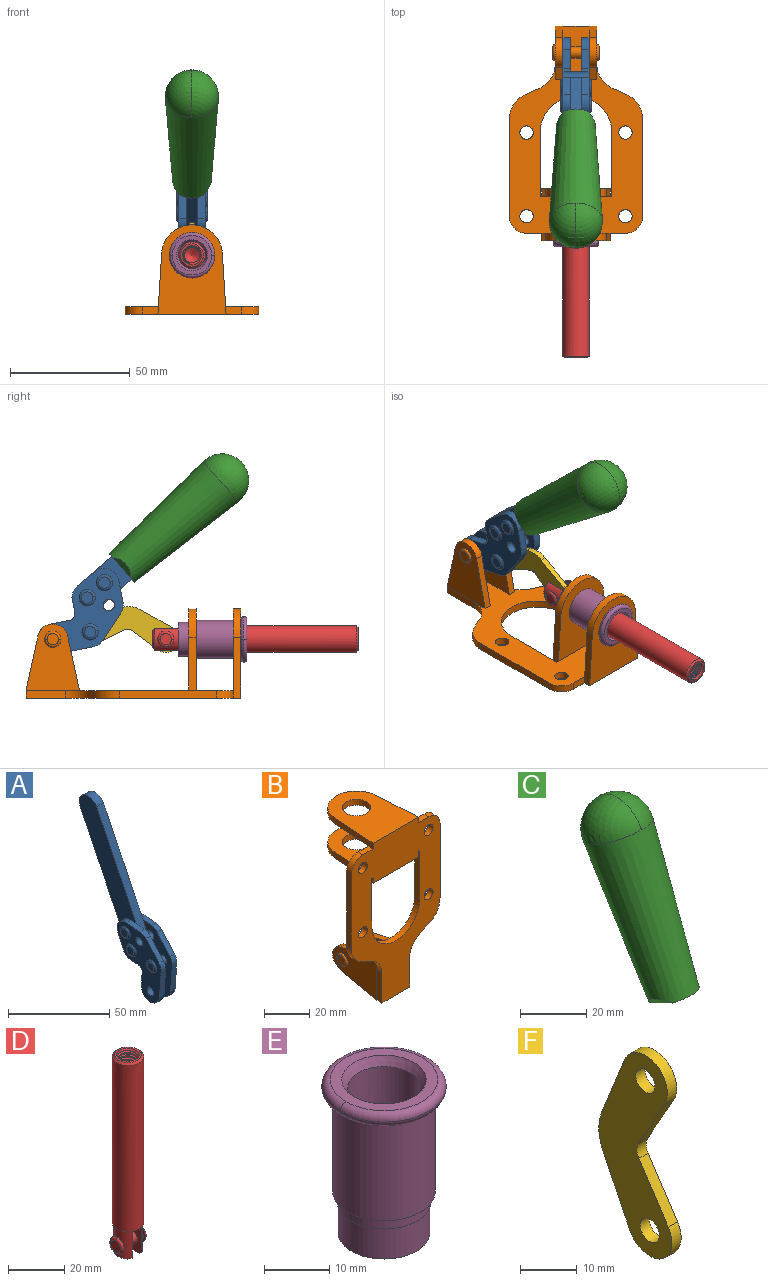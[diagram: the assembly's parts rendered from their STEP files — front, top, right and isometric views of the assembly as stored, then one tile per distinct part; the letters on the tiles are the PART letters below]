
ASSEMBLY  parts=6 mates=6
PART A: 59 faces, bbox 12.9x60.2x99.6 mm
  f0: torus R=2.39mm, axis (-1,0,0), area 14.9mm2, adj f20,f43,f51
  f1: torus R=2.39mm, axis (-1,0,0), area 14.9mm2, adj f19,f42,f51
  f2: torus R=2.39mm, axis (-1,0,0), area 14.9mm2, adj f18,f35,f51
  f3: torus R=2.39mm, axis (-1,0,0), area 14.9mm2, adj f14,f17,f23
  f4: torus R=2.39mm, axis (-1,0,0), area 14.9mm2, adj f13,f16,f23
  f5: torus R=2.39mm, axis (-1,0,0), area 14.9mm2, adj f12,f15,f23
  f6: cylinder r=2.39mm len=4.78mm, axis (1,0,0), area 46.5mm2, adj f48,f50,f51
  f7: cylinder r=2.39mm len=4.78mm, axis (1,0,0), area 46.5mm2, adj f50,f51
  f8: cylinder r=6.35mm len=12.68mm, axis (1,0,0), area 61.8mm2, adj f38,f39,f50,f51
  f9: cylinder r=2.39mm len=4.78mm, axis (-1,0,0), area 70.5mm2, adj f46,f50
  f10: cylinder r=2.39mm len=4.78mm, axis (-1,0,0), area 46.5mm2, adj f23,f45,f46
  f11: cylinder r=2.39mm len=4.78mm, axis (-1,0,0), area 46.5mm2, adj f23,f46
  f12: plane 4.78x4.78mm, normal (1,0,0), area 17.9mm2, adj f5,f15
  f13: plane 4.78x4.78mm, normal (1,0,0), area 17.9mm2, adj f4,f16
  f14: plane 4.78x4.78mm, normal (1,0,0), area 17.9mm2, adj f3,f17
  f15: torus R=2.39mm, axis (-1,0,0), area 14.9mm2, adj f5,f12,f23
  f16: torus R=2.39mm, axis (-1,0,0), area 14.9mm2, adj f4,f13,f23
  f17: torus R=2.39mm, axis (-1,0,0), area 14.9mm2, adj f3,f14,f23
  f18: plane 4.78x4.78mm, normal (-1,0,0), area 17.9mm2, adj f2,f35
  f19: plane 4.78x4.78mm, normal (-1,0,0), area 17.9mm2, adj f1,f42
  f20: plane 4.78x4.78mm, normal (-1,0,0), area 17.9mm2, adj f0,f43
  f21: plane 2.26x0.2mm, normal (1,0,0), area 0.2mm2, adj f31,f44
  f22: plane 2.26x0.2mm, normal (-1,0,0), area 0.2mm2, adj f41,f44
  f23: plane 39.37x30.77mm, normal (1,0,0), area 565.5mm2, adj f3,f4,f5,f10,f11,f15,f16,f17
  f24: cylinder r=6.1mm len=4.15mm, axis (-1,0,0), area 14.7mm2, adj f23,f25,f32,f46
  f25: plane 10.25x9.01mm, normal (0,-0.75,0.66), area 42.3mm2, adj f23,f24,f26,f46
  f26: cylinder r=6.35mm len=4.64mm, axis (-1,0,0), area 15.6mm2, adj f23,f25,f27,f46
  f27: plane 15.84x3.1mm, normal (0,-1,-0.07), area 49.2mm2, adj f23,f26,f28,f46
  f28: cylinder r=6.35mm len=12.68mm, axis (-1,0,0), area 61.8mm2, adj f23,f27,f29,f46
  f29: plane 8.11x3.1mm, normal (0,1,0.07), area 25.2mm2, adj f23,f28,f30,f46
  f30: cylinder r=3.05mm len=3.25mm, axis (-1,0,0), area 14.8mm2, adj f23,f29,f31,f46
  f31: plane 5.99x3.1mm, normal (0,0.07,-1), area 18.6mm2, adj f21,f23,f30,f44,f46
  f32: plane 9.5x3.1mm, normal (0,-0.07,1), area 29.5mm2, adj f23,f24,f33,f46,f47
  f33: cylinder r=6.1mm len=8.63mm, axis (-1,0,0), area 39.1mm2, adj f23,f32,f34,f47
  f34: plane 8.65x3.96mm, normal (0,0.91,-0.42), area 29.5mm2, adj f23,f33,f44,f47
  f35: torus R=2.39mm, axis (-1,0,0), area 14.9mm2, adj f2,f18,f51
  f36: plane 10.25x9.01mm, normal (0,-0.75,0.66), area 42.3mm2, adj f37,f49,f50,f51
  f37: cylinder r=6.35mm len=4.64mm, axis (1,0,0), area 15.6mm2, adj f36,f38,f50,f51
  f38: plane 15.84x3.1mm, normal (0,-1,-0.07), area 49.2mm2, adj f8,f37,f50,f51
  f39: plane 8.11x3.1mm, normal (0,1,0.07), area 25.2mm2, adj f8,f40,f50,f51
  f40: cylinder r=3.05mm len=3.25mm, axis (1,0,0), area 14.8mm2, adj f39,f41,f50,f51
  f41: plane 5.99x3.1mm, normal (0,0.07,-1), area 18.6mm2, adj f22,f40,f44,f50,f51
  f42: torus R=2.39mm, axis (-1,0,0), area 14.9mm2, adj f1,f19,f51
  f43: torus R=2.39mm, axis (-1,0,0), area 14.9mm2, adj f0,f20,f51
  f44: cylinder r=6.35mm len=12.12mm, axis (-1,0,0), area 128.9mm2, adj f21,f22,f23,f31,f34,f41,f46,f47
  f45: plane 2.65x1.35mm, normal (1,0,0), area 1mm2, adj f10,f55
  f46: plane 39.08x20.42mm, normal (-1,0,0), area 412.5mm2, adj f9,f10,f11,f24,f25,f26,f27,f28
  f47: plane 77.62x39.82mm, normal (1,0,0), area 850mm2, adj f32,f33,f34,f44,f53,f54,f55
  f48: plane 2.65x1.35mm, normal (-1,0,0), area 1mm2, adj f6,f55
  f49: cylinder r=6.1mm len=4.15mm, axis (1,0,0), area 14.7mm2, adj f36,f50,f51,f56
  f50: plane 39.08x20.42mm, normal (1,0,0), area 412.5mm2, adj f6,f7,f8,f9,f36,f37,f38,f39
  f51: plane 39.37x30.77mm, normal (-1,0,0), area 565.5mm2, adj f0,f1,f2,f6,f7,f8,f35,f36
  f52: plane 8.65x3.96mm, normal (0,0.91,-0.42), area 29.5mm2, adj f44,f51,f57,f58
  f53: plane 68.49x33.4mm, normal (0,0.9,-0.44), area 358.1mm2, adj f44,f47,f54,f58
  f54: cylinder r=6.35mm len=12.06mm, axis (1,0,0), area 93.7mm2, adj f47,f53,f55,f58
  f55: plane 68.49x33.4mm, normal (0,-0.9,0.44), area 358.1mm2, adj f44,f45,f46,f47,f48,f50,f54,f58
  f56: plane 9.5x3.1mm, normal (0,-0.07,1), area 29.5mm2, adj f49,f50,f51,f57,f58
  f57: cylinder r=6.1mm len=8.63mm, axis (1,0,0), area 39.1mm2, adj f51,f52,f56,f58
  f58: plane 77.62x39.82mm, normal (-1,0,0), area 850mm2, adj f44,f52,f53,f54,f55,f56,f57
PART B: 55 faces, bbox 55.7x37.4x89.8 mm
  f0: torus R=2.41mm, axis (-1,0,0), area 15mm2, adj f11,f15,f25
  f1: torus R=2.41mm, axis (-1,0,0), area 15mm2, adj f10,f12,f22
  f2: cylinder r=2.78mm len=5.56mm, axis (0,-1,0), area 54.2mm2, adj f30,f54
  f3: cylinder r=14.99mm len=29.97mm, axis (0,-1,0), area 145.9mm2, adj f30,f49,f53,f54
  f4: cylinder r=2.78mm len=5.56mm, axis (0,-1,0), area 54.2mm2, adj f30,f54
  f5: cylinder r=2.78mm len=5.56mm, axis (0,-1,0), area 54.2mm2, adj f30,f54
  f6: cylinder r=2.78mm len=5.56mm, axis (0,-1,0), area 54.2mm2, adj f30,f54
  f7: cylinder r=6.35mm len=12.7mm, axis (0,0,1), area 123.6mm2, adj f27,f51
  f8: cylinder r=6.35mm len=12.7mm, axis (0,0,-1), area 124.7mm2, adj f21,f35
  f9: cylinder r=2.41mm len=11.18mm, axis (-1,0,0), area 169.4mm2, adj f16,f19
  f10: plane 4.83x4.83mm, normal (1,0,0), area 18.3mm2, adj f1,f12
  f11: plane 4.83x4.83mm, normal (-1,0,0), area 18.3mm2, adj f0,f15
  f12: torus R=2.41mm, axis (-1,0,0), area 15mm2, adj f1,f10,f22
  f13: cylinder r=6.35mm len=12.41mm, axis (1,0,0), area 53.4mm2, adj f18,f19,f22,f23
  f14: cylinder r=6.35mm len=12.41mm, axis (-1,0,0), area 53.4mm2, adj f16,f17,f24,f25
  f15: torus R=2.41mm, axis (-1,0,0), area 15mm2, adj f0,f11,f25
  f16: plane 27.86x22.35mm, normal (1,0,0), area 425.4mm2, adj f9,f14,f17,f24,f30
  f17: plane 22.86x4.97mm, normal (0,0.21,0.98), area 72.5mm2, adj f14,f16,f25,f30
  f18: plane 22.86x4.97mm, normal (0,0.21,0.98), area 72.5mm2, adj f13,f19,f22,f30
  f19: plane 27.86x22.35mm, normal (-1,0,0), area 425.4mm2, adj f9,f13,f18,f23,f30
  f20: cylinder r=12.7mm len=25.35mm, axis (0,0,-1), area 119.8mm2, adj f21,f34,f35,f36
  f21: plane 34.21x28.07mm, normal (0,0,-1), area 702.4mm2, adj f8,f20,f30,f34,f36
  f22: plane 27.96x22.45mm, normal (1,0,0), area 407.2mm2, adj f1,f12,f13,f18,f23,f30,f42,f43
  f23: plane 22.86x4.97mm, normal (0,0.21,-0.98), area 72.5mm2, adj f13,f19,f22,f44
  f24: plane 22.86x4.97mm, normal (0,0.21,-0.98), area 72.5mm2, adj f14,f16,f25,f44
  f25: plane 27.86x22.35mm, normal (-1,0,0), area 407.1mm2, adj f0,f14,f15,f17,f24,f30,f45,f46
  f26: plane 3.1x0.95mm, normal (0,0,-1), area 2.7mm2, adj f30,f49,f50,f54
  f27: plane 34.21x28.07mm, normal (0,0,1), area 702.4mm2, adj f7,f28,f30,f50,f52
  f28: cylinder r=12.7mm len=25.35mm, axis (0,0,1), area 118.8mm2, adj f27,f50,f51,f52
  f29: plane 3.1x0.95mm, normal (0,0,-1), area 2.7mm2, adj f30,f52,f53,f54
  f30: plane 86.54x55.63mm, normal (0,1,0), area 2362.9mm2, adj f2,f3,f4,f5,f6,f16,f17,f18
  f31: plane 40.56x3.1mm, normal (-1,0,0), area 125.7mm2, adj f30,f32,f48,f54
  f32: cylinder r=7.11mm len=7.11mm, axis (0,-1,0), area 34.6mm2, adj f30,f31,f33,f54
  f33: plane 6.67x3.1mm, normal (0,0,1), area 20.4mm2, adj f30,f32,f34,f54
  f34: plane 25.39x3.13mm, normal (-1,0.06,0), area 79.5mm2, adj f20,f21,f33,f35,f54
  f35: plane 37.31x28.45mm, normal (0,0,1), area 789.9mm2, adj f8,f20,f34,f36,f54
  f36: plane 25.39x3.13mm, normal (1,0.06,0), area 79.5mm2, adj f20,f21,f35,f37,f54
  f37: plane 6.67x3.1mm, normal (0,0,1), area 20.4mm2, adj f30,f36,f38,f54
  f38: cylinder r=7.11mm len=7.11mm, axis (0,-1,0), area 34.6mm2, adj f30,f37,f39,f54
  f39: plane 40.56x3.1mm, normal (1,0,0), area 125.7mm2, adj f30,f38,f40,f54
  f40: cylinder r=11.18mm len=10.16mm, axis (0,-1,0), area 39.5mm2, adj f30,f39,f41,f54
  f41: plane 6.09x3.1mm, normal (0.42,0,-0.91), area 20.8mm2, adj f30,f40,f42,f54
  f42: cylinder r=11.18mm len=9.41mm, axis (0,-1,0), area 37.2mm2, adj f22,f30,f41,f43,f54
  f43: plane 16.5x3.1mm, normal (1,0,0), area 51.1mm2, adj f22,f42,f44,f54
  f44: plane 17.37x3.1mm, normal (0,0,-1), area 53.8mm2, adj f23,f24,f30,f43,f45,f54
  f45: plane 16.5x3.1mm, normal (-1,0,0), area 51.1mm2, adj f25,f44,f46,f54
  f46: cylinder r=11.18mm len=9.41mm, axis (0,-1,0), area 37.2mm2, adj f25,f30,f45,f47,f54
  f47: plane 6.09x3.1mm, normal (-0.42,0,-0.91), area 20.8mm2, adj f30,f46,f48,f54
  f48: cylinder r=11.18mm len=10.16mm, axis (0,-1,0), area 39.5mm2, adj f30,f31,f47,f54
  f49: plane 26.54x3.1mm, normal (-1,0,0), area 82.3mm2, adj f3,f26,f30,f54
  f50: plane 25.39x3.1mm, normal (1,0.06,0), area 78.8mm2, adj f26,f27,f28,f51,f54
  f51: plane 37.31x28.45mm, normal (0,0,-1), area 789.9mm2, adj f7,f28,f50,f52,f54
  f52: plane 25.39x3.1mm, normal (-1,0.06,0), area 78.8mm2, adj f27,f28,f29,f51,f54
  f53: plane 26.54x3.1mm, normal (1,0,0), area 82.3mm2, adj f3,f29,f30,f54
  f54: plane 89.66x55.63mm, normal (0,-1,0), area 2678.5mm2, adj f2,f3,f4,f5,f6,f26,f29,f31
PART C: 11 faces, bbox 22.3x42.6x64.5 mm
  f0: sphere r=11.13mm, area 411.4mm2, adj f1,f8
  f1: cone r=11.11mm half-angle=3.3deg, axis (0,0.44,0.9), area 3251.8mm2, adj f0,f7,f8,f9,f10
  f2: cylinder r=6.16mm len=11.7mm, axis (1,0,0), area 89.5mm2, adj f3,f4,f5,f6
  f3: plane 60.23x36.75mm, normal (-1,0,0), area 763.6mm2, adj f2,f4,f6,f10
  f4: plane 51.37x25.05mm, normal (0,0.9,-0.44), area 264.2mm2, adj f2,f3,f5,f10
  f5: plane 60.23x36.75mm, normal (1,0,0), area 763.6mm2, adj f2,f4,f6,f10
  f6: plane 51.37x25.05mm, normal (0,-0.9,0.44), area 264.2mm2, adj f2,f3,f5,f10
  f7: plane 9.95x5.95mm, normal (0.71,-0.31,-0.64), area 25.8mm2, adj f1,f10
  f8: sphere r=11.13mm, area 411.4mm2, adj f0,f1
  f9: plane 9.95x5.95mm, normal (-0.71,-0.31,-0.64), area 25.8mm2, adj f1,f10
  f10: plane 14.27x11.38mm, normal (0,-0.44,-0.9), area 106.7mm2, adj f1,f3,f4,f5,f6,f7,f9
PART D: 48 faces, bbox 12.6x11.1x86.1 mm
  f0: torus R=2.41mm, axis (-1,0,0), area 15mm2, adj f30,f32,f34
  f1: torus R=2.41mm, axis (-1,0,0), area 15mm2, adj f29,f31,f33
  f2: cylinder r=5.54mm len=72.39mm, axis (0,0,1), area 2518.5mm2, adj f3,f4,f42,f43
  f3: cone r=5.54mm half-angle=45deg, axis (0,0,1), area 7.6mm2, adj f2,f5,f41
  f4: cone r=5.54mm half-angle=45deg, axis (0,0,-1), area 34.9mm2, adj f2,f39
  f5: cylinder r=5.08mm len=11.48mm, axis (0,0,1), area 108.3mm2, adj f3,f7,f8,f41
  f6: cylinder r=2.41mm len=4.83mm, axis (-1,0,0), area 71.2mm2, adj f40,f41
  f7: cylinder r=2.41mm len=4.83mm, axis (-1,0,0), area 7.6mm2, adj f5,f34
  f8: cone r=5.08mm half-angle=45deg, axis (0,0,1), area 10.6mm2, adj f5,f37,f41
  f9: cone r=3.98mm half-angle=45deg, axis (0,0,1), area 17.6mm2, adj f27,f39,f45,f46,f47
  f10: cylinder r=2.41mm len=4.83mm, axis (-1,0,0), area 7.6mm2, adj f33,f38
  f11: cylinder r=3.2mm len=6.4mm, axis (0,0,1), area 78.4mm2, adj f12,f28,f44,f45,f47
  f12: cylinder r=3.2mm len=6.4mm, axis (0,0,1), area 10.5mm2, adj f11,f13,f45,f47
  f13: cylinder r=3.2mm len=6.4mm, axis (0,0,1), area 10.5mm2, adj f12,f14,f45,f47
  f14: cylinder r=3.2mm len=6.4mm, axis (0,0,1), area 10.5mm2, adj f13,f15,f45,f47
  f15: cylinder r=3.2mm len=6.4mm, axis (0,0,1), area 10.5mm2, adj f14,f16,f45,f47
  f16: cylinder r=3.2mm len=6.4mm, axis (0,0,1), area 10.5mm2, adj f15,f17,f45,f47
  f17: cylinder r=3.2mm len=6.4mm, axis (0,0,1), area 10.5mm2, adj f16,f18,f45,f47
  f18: cylinder r=3.2mm len=6.4mm, axis (0,0,1), area 10.5mm2, adj f17,f19,f45,f47
  f19: cylinder r=3.2mm len=6.4mm, axis (0,0,1), area 10.5mm2, adj f18,f20,f45,f47
  f20: cylinder r=3.2mm len=6.4mm, axis (0,0,1), area 10.5mm2, adj f19,f21,f45,f47
  f21: cylinder r=3.2mm len=6.4mm, axis (0,0,1), area 10.5mm2, adj f20,f22,f45,f47
  f22: cylinder r=3.2mm len=6.4mm, axis (0,0,1), area 10.5mm2, adj f21,f23,f45,f47
  f23: cylinder r=3.2mm len=6.4mm, axis (0,0,1), area 10.5mm2, adj f22,f24,f45,f47
  f24: cylinder r=3.2mm len=6.4mm, axis (0,0,1), area 10.5mm2, adj f23,f25,f45,f47
  f25: cylinder r=3.2mm len=6.4mm, axis (0,0,1), area 10.5mm2, adj f24,f26,f45,f47
  f26: cylinder r=3.2mm len=6.4mm, axis (0,0,1), area 10.5mm2, adj f25,f27,f45,f47
  f27: cylinder r=3.2mm len=6.4mm, axis (0,0,1), area 7.4mm2, adj f9,f26,f45,f47
  f28: cone r=3.2mm half-angle=60deg, axis (0,0,1), area 37.2mm2, adj f11
  f29: plane 4.83x4.83mm, normal (-1,0,0), area 18.3mm2, adj f1,f31
  f30: plane 4.83x4.83mm, normal (1,0,0), area 18.3mm2, adj f0,f32
  f31: torus R=2.41mm, axis (-1,0,0), area 15mm2, adj f1,f29,f33
  f32: torus R=2.41mm, axis (-1,0,0), area 15mm2, adj f0,f30,f34
  f33: plane 6.83x6.83mm, normal (1,0,0), area 18.3mm2, adj f1,f10,f31
  f34: plane 6.83x6.83mm, normal (-1,0,0), area 18.3mm2, adj f0,f7,f32
  f35: cone r=5.08mm half-angle=45deg, axis (0,0,1), area 10.6mm2, adj f36,f38,f40
  f36: plane 7.25x1.97mm, normal (0,0,-1), area 10mm2, adj f35,f40
  f37: plane 7.25x1.97mm, normal (0,0,-1), area 10mm2, adj f8,f41
  f38: cylinder r=5.08mm len=11.48mm, axis (0,0,1), area 108.3mm2, adj f10,f35,f40,f42
  f39: plane 9.55x9.55mm, normal (0,0,1), area 22mm2, adj f4,f9
  f40: plane 12.76x10.09mm, normal (1,0,0), area 95.7mm2, adj f6,f35,f36,f38,f42,f43
  f41: plane 12.76x10.09mm, normal (-1,0,0), area 95.7mm2, adj f3,f5,f6,f8,f37,f43
  f42: cone r=5.54mm half-angle=45deg, axis (0,0,1), area 7.6mm2, adj f2,f38,f40
  f43: plane 11.07x4.7mm, normal (0,0,-1), area 50.4mm2, adj f2,f40,f41
  f44: plane 0.89x0.62mm, normal (-1,0,0), area 0.3mm2, adj f11,f45,f46,f47
  f45: bspline ~24.8x7.63mm, area 266.6mm2, adj f9,f11,f12,f13,f14,f15,f16,f17
  f46: bspline ~24.87x7.63mm, area 73.6mm2, adj f9,f44,f45,f47
  f47: bspline ~24.98x7.63mm, area 272.5mm2, adj f9,f11,f12,f13,f14,f15,f16,f17
PART E: 15 faces, bbox 20.6x20.6x28.7 mm
  f0: torus R=8.26mm, axis (0,0,1), area 56.8mm2, adj f1,f10,f12
  f1: torus R=8.26mm, axis (0,0,1), area 56.8mm2, adj f0,f6,f13
  f2: cylinder r=5.59mm len=25.91mm, axis (0,0,1), area 909.6mm2, adj f3,f4
  f3: cone r=6.86mm half-angle=45deg, axis (0,0,-1), area 70.2mm2, adj f2,f14
  f4: cone r=6.47mm half-angle=30deg, axis (0,0,1), area 66.7mm2, adj f2,f13
  f5: cylinder r=7.04mm len=14.07mm, axis (0,0,1), area 252.6mm2, adj f11,f14
  f6: torus R=8.26mm, axis (0,0,1), area 56.8mm2, adj f1,f12,f13
  f7: cylinder r=7.16mm len=14.33mm, axis (0,0,1), area 91.5mm2, adj f9,f11
  f8: cylinder r=7.86mm len=18.42mm, axis (0,0,1), area 909.6mm2, adj f9,f10
  f9: plane 15.72x15.72mm, normal (0,0,-1), area 33mm2, adj f7,f8
  f10: plane 16.51x16.51mm, normal (0,0,-1), area 19.9mm2, adj f0,f8,f12
  f11: plane 14.33x14.33mm, normal (0,0,-1), area 5.7mm2, adj f5,f7
  f12: torus R=8.26mm, axis (0,0,1), area 56.8mm2, adj f0,f6,f10
  f13: plane 16.51x16.51mm, normal (0,0,1), area 82.7mm2, adj f1,f4,f6
  f14: plane 14.07x14.07mm, normal (0,0,-1), area 7.8mm2, adj f3,f5
PART F: 12 faces, bbox 2.3x18.2x42.8 mm
  f0: cylinder r=2.4mm len=4.8mm, axis (1,0,0), area 34.9mm2, adj f4,f11
  f1: cylinder r=10.41mm len=8.47mm, axis (1,0,0), area 20.2mm2, adj f4,f9,f10,f11
  f2: cylinder r=3.05mm len=3.16mm, axis (1,0,0), area 7.7mm2, adj f4,f6,f7,f11
  f3: cylinder r=2.4mm len=4.8mm, axis (1,0,0), area 34.9mm2, adj f4,f11
  f4: plane 42.81x18.23mm, normal (-1,0,0), area 414.1mm2, adj f0,f1,f2,f3,f5,f6,f7,f8
  f5: cylinder r=5.54mm len=10.67mm, axis (1,0,0), area 41.8mm2, adj f4,f6,f10,f11
  f6: plane 11.66x6.53mm, normal (0,-0.87,-0.49), area 30.9mm2, adj f2,f4,f5,f11
  f7: plane 11.17x7.33mm, normal (0,-0.84,0.55), area 30.9mm2, adj f2,f4,f8,f11
  f8: cylinder r=5.54mm len=10.51mm, axis (1,0,0), area 41.8mm2, adj f4,f7,f9,f11
  f9: plane 13.67x6.67mm, normal (0,0.9,-0.44), area 35.1mm2, adj f1,f4,f8,f11
  f10: plane 14.1x5.7mm, normal (0,0.93,0.37), area 35.1mm2, adj f1,f4,f5,f11
  f11: plane 42.81x18.23mm, normal (1,0,0), area 414.1mm2, adj f0,f1,f2,f3,f5,f6,f7,f8
PLACE A rot(axis=(1,0,0),75deg) t=(0,3.86,9.14)mm
PLACE B rot(axis=(1,0,0),90deg) t=(0,9.14,0)mm fixed
PLACE C rot(axis=(1,0,0),75deg) t=(-0.04,3.86,9.14)mm
PLACE D rot(axis=(1,0,0),90deg) t=(0,9.52,0)mm
PLACE E rot(axis=(1,0,0),90deg) t=(0,9.14,0)mm
PLACE F rot(axis=(1,0,0),97.5deg) t=(0,12.59,2.22)mm
MATE fastened C.f2 <-> A.f54  axis (1,0,0) through (-2.35,-30.66,91.94)mm
MATE revolute F.f5 <-> D.f6  axis (1,0,0) through (0,-5.96,24.61)mm
MATE slider D.f2 <-> E.f2  axis (0,-1,0) through (0,-49.26,24.61)mm
MATE revolute B.f0 <-> A.f7  axis (-1,0,0) through (0,41.23,24.61)mm
MATE revolute F.f3 <-> A.f4  axis (1,0,0) through (0,25.65,27.64)mm
MATE fastened B.f7 <-> E.f2  axis (0,-1,0) through (0,-37.25,24.61)mm
